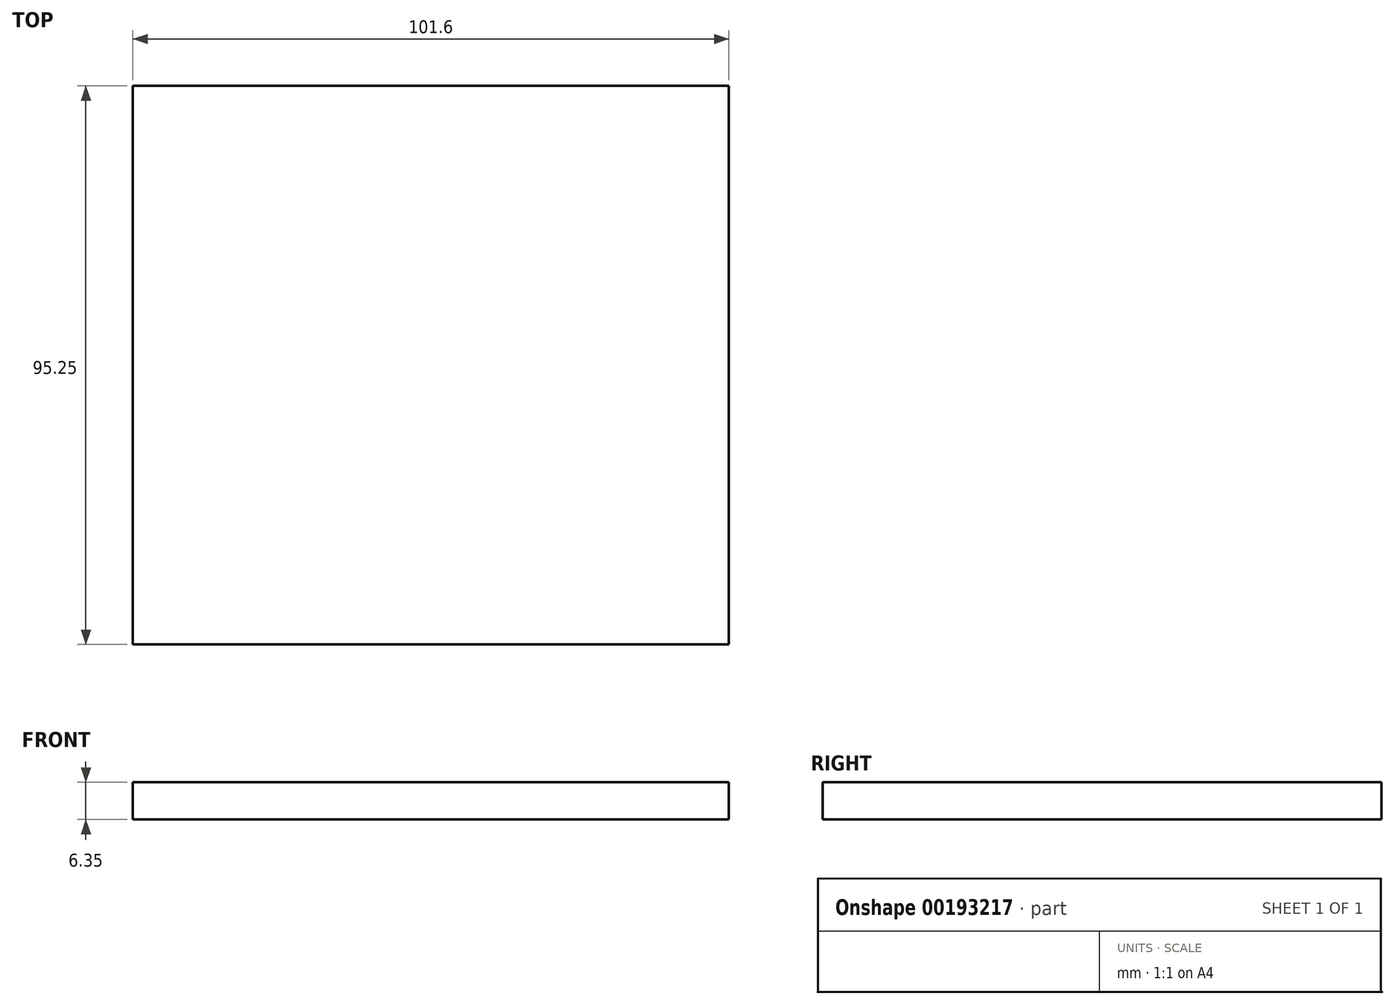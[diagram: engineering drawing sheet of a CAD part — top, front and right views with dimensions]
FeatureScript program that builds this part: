
annotation { "Feature Type Name" : "Feature", "Feature Type Description" : "" }
export const myFeature = defineFeature(function(context is Context, id is Id, definition is map)
    precondition{}
    {
        {
            var Q0;
            Q0=qCreatedBy(makeId("Top.planeOp"),FACE);
            var sketch = newSketch(context, id + "F0", { "sketchPlane" : qUnion([Q0])});
            skLineSegment(sketch, "E0.bottom", {"start": v(-48.6, 32.18) * mm, "end": v(53, 32.18) * mm});
            skLineSegment(sketch, "E0.top", {"start": v(-48.6, -63.07) * mm, "end": v(53, -63.07) * mm});
            skLineSegment(sketch, "E0.left", {"start": v(-48.6, 32.18) * mm, "end": v(-48.6, -63.07) * mm});
            skLineSegment(sketch, "E0.right", {"start": v(53, 32.18) * mm, "end": v(53, -63.07) * mm});
            skSolve(sketch);
        }
        {
            var Q0;
            Q0 = qSketchRegion(id + "F0", true);
            extrude(context, id + "F1", {"entities" : qUnion([Q0]), "depth" : 6.35 * mm});
        }
    });
